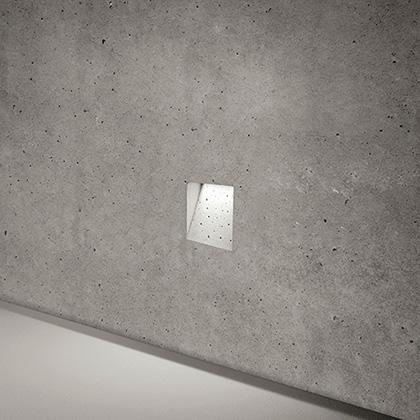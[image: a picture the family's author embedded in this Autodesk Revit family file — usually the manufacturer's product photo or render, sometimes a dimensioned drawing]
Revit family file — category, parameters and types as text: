
# Revit family: SIMES_C.8030W_Ghost
name_source: partatom
category: Lighting Fixtures
revit_build: Autodesk Revit 2016 (Build: 20150714_1515(x64)
units: mm (PartAtom-declared; Revit-internal decimal feet)

## family parameters
Cut with Voids When Loaded = No
Host = Face
Light Source = Yes
Part Type = Normal
Room Calculation Point = No
Round Connector Dimension = Use Diameter
Shared = No

## types (1)
- SIMES_C.8030W_Ghost
    Approval mark = CE
    Assembly Code = D5020
    Color Filter = 16777215
    Color Rendering Index = CRI 80
    Colour Temperature = 3000
    Control Gear = none
    Default Elevation = 1219 mm
    Description = MICROGHOST SQUARE
Art. C.8030W
MODULES LED 3000K  24V CRI 80
Rated luminaire luminous flux: 240lm
Rated input power: 4W
Luminaire efficacy: 60lm/W
Without trasformer
CE

PRODUCT TYPE
Wall mounted luminaire. IP rating IP 65
MATERIAL CHARACTERISTICS
Ghost is a lighting void that is obtained from a polypropylene housing anchored to the retaining panels before pouring the concrete. Ghost is composed of two elements: the housing and the lighting element. The housing is in polypropylene and it consists of two complementary parts: - A jig , which forms the housing, and is extracted together with the retaining panel after completing the casting and removing the anchor screws; - The housing  that remains embedded inside the casting and houses the lighting element. (The housing is supplied with bolts, locking system and stickers to be applied on the outside of the retaining panels so to secure a perfect alignment for multiple installations of each housing when pouring the concrete). The lighting element in die cast aluminum is anchored to the casing  through proper screws and it remains completely hided into the void. Mechanical resistance IK 06
MAINTENANCE
This product is manufactured on site during the concrete casting of the wall with hand crafted procedures; therefore, small imperfections caused by the low accurance of the casting, subsidence of the concrete surface, actual and future cracks, colour ripples and variations over time, will be deliberately present and they are a feature of the concrete, proving the hand-made manufacturing procedure.
LIGHTING PERFORMANCE
Toughened glass diffuser. LOR -- 
WIRING
Supplied with a pre-wired 3m H05RN-F cable. Isolation: CLASS III . Available colours: Cast cement. Weight:  Kg Glow Wire test: --
L.E.D circuit included.
GHOST PATENDED, REGISTERED DESIGN
This luminaire contains built-in LED modules with energy class: A, A+, A++. In case of damage or malfunction please contact the manufacturer to receive additional instructions on how to replace and relative spare parts to order. The LED modules cannot be handled in the luminaire by the end user (Regulation UE 874/2012).
LED circuit boards are engineered accordingly to actual Lumen Maintenance regulation (LM80) and Technical Memorandum (TM21) where uniformity and quality of light is 50.000 hours referred to L70  B20 Ta 25°C.Lifecycle refers to LED circuit boards only, all others components of the luminaire are excluded.

EMERGENCY VERSIONS The fittings operates both on AC ( 50/60Hz ) and DC ( 0Hz ) voltage.
    Dimming Lamp Color Temperature Shift = <None>
    IFC Classification = Light Fixture
    IK Rating = IK 06
    Lamp = LED
    Lamp Light Flux = 320
    Lamp count = 1
    Last Update = 02/08/2018 10:21:49
    Lifetime = 50000 L70 B20 Ta 25°C
    Light Output Ratio = 100
    Luminous efficacy = 60
    Manufacturer = SIMES
    Masterformat 2014 Code = 26 56 00
    Masterformat 2014 Description = Exterior Lighting
    Model = C.8030W
    Mounting Place = Wall
    Mounting Type = Recessed
    NBS Reference Code = 49
    NBS Reference Description = Luminaries And Lamps
    OmniClass Code = 23-35 47 11
    OmniClass Description = Lighting Fixture
    Photometric Web File = C8030W.ies
    Product Group = recessed luminaire
    Product Name = Ghost for cast concrete
    Protection Class = Safety extra-low voltage
    Protection Degree = IP 65
    System Light Flux = 240
    System Power = 4
    Tilt Angle = 0.00°
    Type Comments = SIMES S.p.A. - All rights reserved
    Type Image = microghost-quadrato.jpg
    UNSPSC Code = 3911
    URL = http://www.simes.it
    Uniclass 1.4 Code = YJ73
    Uniclass 1.4 Description = Luminaries and lamps
    Uniclass 2.0 Code = PR-49
    Uniclass 2.0 Description = Luminaries and lamps
    Uniclass 2015 Code = EF_70_80
    Uniclass 2015 Name = Lighting
    Uniformat II Code = D5020
    Uniformat II Description = Lighting & Branch Wiring
    Voltage = 24V
    Wattage Comments = 18.0W
